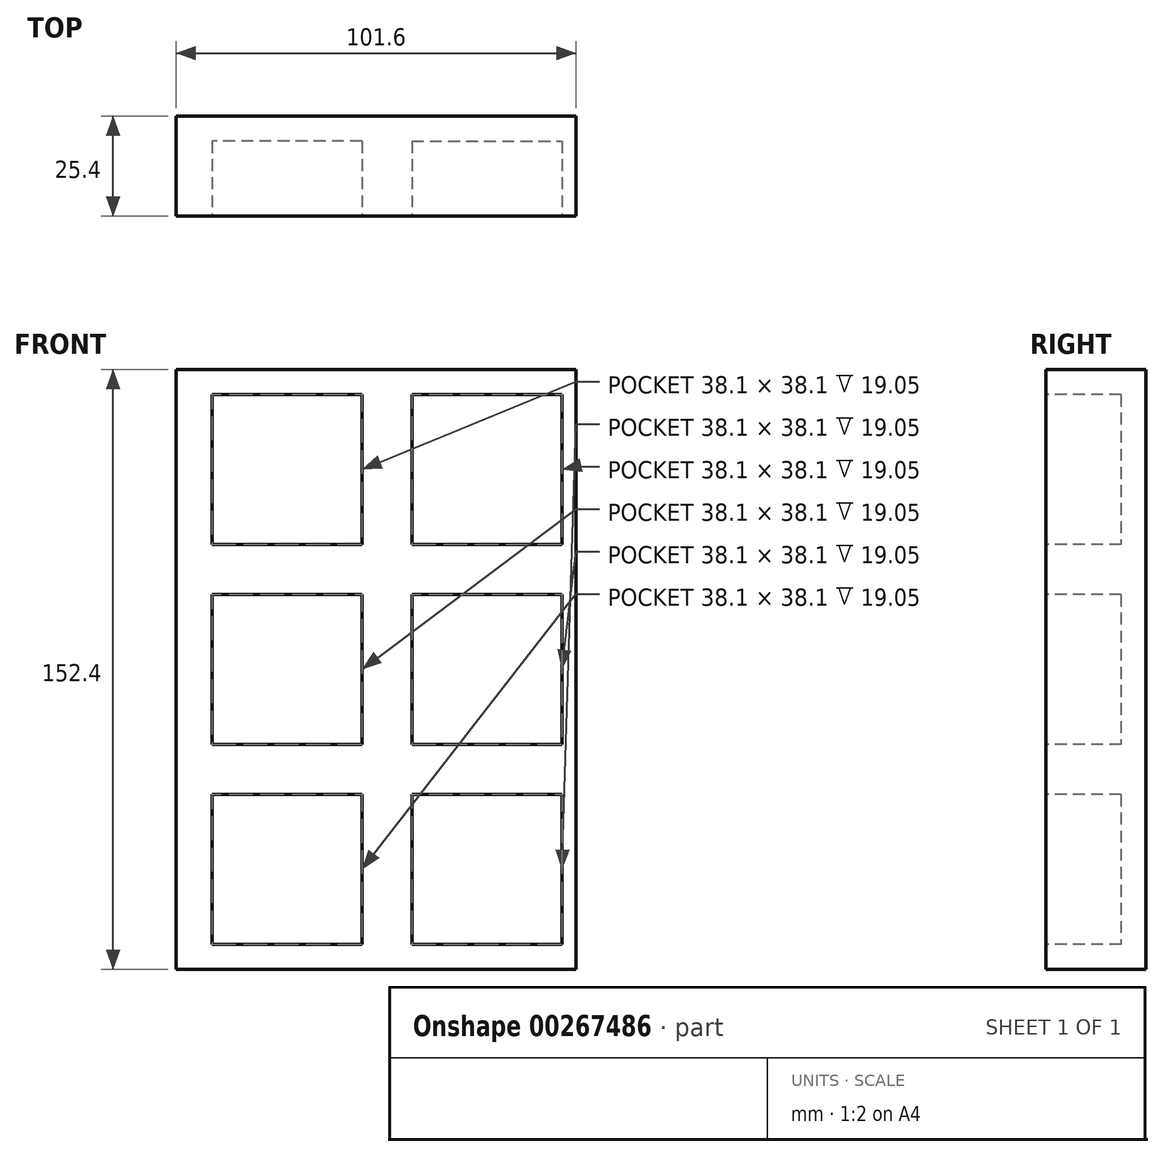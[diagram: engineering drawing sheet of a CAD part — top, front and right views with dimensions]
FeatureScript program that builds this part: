
annotation { "Feature Type Name" : "Feature", "Feature Type Description" : "" }
export const myFeature = defineFeature(function(context is Context, id is Id, definition is map)
    precondition{}
    {
        {
            var Q0;
            Q0=qCreatedBy(makeId("Front.planeOp"),FACE);
            var sketch = newSketch(context, id + "F0", { "sketchPlane" : qUnion([Q0])});
            skLineSegment(sketch, "E0.bottom", {"start": v(48.06, 76.2) * mm, "end": v(-53.54, 76.2) * mm});
            skLineSegment(sketch, "E0.top", {"start": v(48.06, -76.2) * mm, "end": v(-53.54, -76.2) * mm});
            skLineSegment(sketch, "E0.left", {"start": v(48.06, 76.2) * mm, "end": v(48.06, -76.2) * mm});
            skLineSegment(sketch, "E0.right", {"start": v(-53.54, 76.2) * mm, "end": v(-53.54, -76.2) * mm});
            skPoint(sketch, "E0.middle", {"position": v(-2.74, 0) * mm});
            skSolve(sketch);
        }
        {
            var Q0;
            Q0=makeQuery(id+"F0.imprint","IMPRINT",FACE,{"disambiguationData":[TD([[makeQuery(id+"F0.imprint","IMPRINT",EDGE,{"derivedFrom":sQuery(id+"F0.wireOp",EDGE,"E0.bottom")}),1.0]])]});
            extrude(context, id + "F1", {"entities" : qUnion([Q0]), "depth" : 25.4 * mm});
        }
        {
            var Q0;
            Q0=makeQuery(id+"F1.opExtrude","CAP_FACE",FACE,{"disambiguationData":[OSD([sQuery(id+"F0.wireOp",EDGE,"E0.bottom"),sQuery(id+"F0.wireOp",EDGE,"E0.top"),sQuery(id+"F0.wireOp",EDGE,"E0.left"),sQuery(id+"F0.wireOp",EDGE,"E0.right")])],"isStart":false});
            var sketch = newSketch(context, id + "F2", { "sketchPlane" : qUnion([Q0])});
            skLineSegment(sketch, "E1.bottom", {"start": v(6.35, 76.2) * mm, "end": v(-6.35, 76.2) * mm});
            skLineSegment(sketch, "E1.top", {"start": v(6.35, -76.2) * mm, "end": v(-6.35, -76.2) * mm});
            skPoint(sketch, "E1.middle", {"position": v(0, 0) * mm});
            skLineSegment(sketch, "E2.bottom", {"start": v(-53.54, 76.2) * mm, "end": v(48.06, 76.2) * mm});
            skLineSegment(sketch, "E2.left", {"start": v(-53.54, 76.2) * mm, "end": v(-53.54, 68.45) * mm});
            skLineSegment(sketch, "E2.right", {"start": v(48.06, 76.2) * mm, "end": v(48.06, 68.45) * mm});
            skLineSegment(sketch, "E3.bottom", {"start": v(-53.54, -76.2) * mm, "end": v(48.06, -76.2) * mm});
            skLineSegment(sketch, "E3.left", {"start": v(-53.54, -76.2) * mm, "end": v(-53.54, -63.5) * mm});
            skLineSegment(sketch, "E3.right", {"start": v(48.06, -76.2) * mm, "end": v(48.06, -63.5) * mm});
            skLineSegment(sketch, "E4.bottom", {"start": v(-53.54, 76.2) * mm, "end": v(-47.2, 76.2) * mm});
            skLineSegment(sketch, "E4.top", {"start": v(-53.54, -76.2) * mm, "end": v(-47.2, -76.2) * mm});
            skLineSegment(sketch, "E4.left", {"start": v(-53.54, 76.2) * mm, "end": v(-53.54, -76.2) * mm});
            skLineSegment(sketch, "E5.bottom", {"start": v(48.06, -76.2) * mm, "end": v(41.7, -76.2) * mm});
            skLineSegment(sketch, "E5.top", {"start": v(48.06, 76.2) * mm, "end": v(41.7, 76.2) * mm});
            skLineSegment(sketch, "E5.left", {"start": v(48.06, -76.2) * mm, "end": v(48.06, 76.2) * mm});
            skLineSegment(sketch, "E6.bottom", {"start": v(-6.35, 19.05) * mm, "end": v(-44.45, 19.05) * mm});
            skLineSegment(sketch, "E6.top", {"start": v(-6.35, -19.05) * mm, "end": v(-44.45, -19.05) * mm});
            skLineSegment(sketch, "E6.left", {"start": v(-6.35, 19.05) * mm, "end": v(-6.35, -19.05) * mm});
            skLineSegment(sketch, "E6.right", {"start": v(-44.45, 19.05) * mm, "end": v(-44.45, -19.05) * mm});
            skPoint(sketch, "E6.middle", {"position": v(-25.4, 0) * mm});
            skPoint(sketch, "E7.endSnap0", {"position": v(-25.4, -19.05) * mm});
            skLineSegment(sketch, "E8.bottom", {"start": v(-6.35, -31.75) * mm, "end": v(-44.45, -31.75) * mm});
            skLineSegment(sketch, "E8.top", {"start": v(-6.35, -69.85) * mm, "end": v(-44.45, -69.85) * mm});
            skLineSegment(sketch, "E8.left", {"start": v(-6.35, -31.75) * mm, "end": v(-6.35, -69.85) * mm});
            skLineSegment(sketch, "E8.right", {"start": v(-44.45, -31.75) * mm, "end": v(-44.45, -69.85) * mm});
            skPoint(sketch, "E8.middle", {"position": v(-25.4, -50.8) * mm});
            skLineSegment(sketch, "E9.bottom", {"start": v(-6.35, 69.85) * mm, "end": v(-44.45, 69.85) * mm});
            skLineSegment(sketch, "E9.top", {"start": v(-6.35, 31.75) * mm, "end": v(-44.45, 31.75) * mm});
            skLineSegment(sketch, "E9.left", {"start": v(-6.35, 69.85) * mm, "end": v(-6.35, 31.75) * mm});
            skLineSegment(sketch, "E9.right", {"start": v(-44.45, 69.85) * mm, "end": v(-44.45, 31.75) * mm});
            skPoint(sketch, "E9.middle", {"position": v(-25.4, 50.8) * mm});
            skPoint(sketch, "E10.MirrorP", {"position": v(25.4, -50.8) * mm});
            skLineSegment(sketch, "E11.MirrorCS", {"start": v(6.35, -19.05) * mm, "end": v(44.45, -19.05) * mm});
            skLineSegment(sketch, "E12.MirrorCS", {"start": v(44.45, -31.75) * mm, "end": v(44.45, -69.85) * mm});
            skLineSegment(sketch, "E13.MirrorCS", {"start": v(6.35, 69.85) * mm, "end": v(6.35, 31.75) * mm});
            skLineSegment(sketch, "E14.MirrorCS", {"start": v(6.35, -69.85) * mm, "end": v(44.45, -69.85) * mm});
            skLineSegment(sketch, "E15.MirrorCS", {"start": v(44.45, 69.85) * mm, "end": v(44.45, 31.75) * mm});
            skLineSegment(sketch, "E16.MirrorCS", {"start": v(6.35, 19.05) * mm, "end": v(44.45, 19.05) * mm});
            skLineSegment(sketch, "E17.MirrorCS", {"start": v(6.35, -31.75) * mm, "end": v(44.45, -31.75) * mm});
            skPoint(sketch, "E18.MirrorP", {"position": v(25.4, -19.05) * mm});
            skPoint(sketch, "E19.MirrorP", {"position": v(25.4, 50.8) * mm});
            skPoint(sketch, "E20.MirrorP", {"position": v(25.4, 0) * mm});
            skLineSegment(sketch, "E21.MirrorCS", {"start": v(6.35, 69.85) * mm, "end": v(44.45, 69.85) * mm});
            skLineSegment(sketch, "E22.MirrorCS", {"start": v(6.35, 19.05) * mm, "end": v(6.35, -19.05) * mm});
            skLineSegment(sketch, "E23.MirrorCS", {"start": v(6.35, -31.75) * mm, "end": v(6.35, -69.85) * mm});
            skLineSegment(sketch, "E24.MirrorCS", {"start": v(6.35, 31.75) * mm, "end": v(44.45, 31.75) * mm});
            skLineSegment(sketch, "E25.MirrorCS", {"start": v(44.45, 19.05) * mm, "end": v(44.45, -19.05) * mm});
            skSolve(sketch);
        }
        {
            var Q0;
            Q0=makeQuery(id+"F2.imprint","IMPRINT",FACE,{"disambiguationData":[TD([[makeQuery(id+"F2.imprint","IMPRINT",EDGE,{"derivedFrom":sQuery(id+"F2.wireOp",EDGE,"E9.bottom")}),1.0]])]});
            var Q1;
            Q1=makeQuery(id+"F2.imprint","IMPRINT",FACE,{"disambiguationData":[TD([[makeQuery(id+"F2.imprint","IMPRINT",EDGE,{"derivedFrom":sQuery(id+"F2.wireOp",EDGE,"E13.MirrorCS")}),1.0]])]});
            var Q2;
            Q2=makeQuery(id+"F2.imprint","IMPRINT",FACE,{"disambiguationData":[TD([[makeQuery(id+"F2.imprint","IMPRINT",EDGE,{"derivedFrom":sQuery(id+"F2.wireOp",EDGE,"E6.bottom")}),1.0]])]});
            var Q3;
            Q3=makeQuery(id+"F2.imprint","IMPRINT",FACE,{"disambiguationData":[TD([[makeQuery(id+"F2.imprint","IMPRINT",EDGE,{"derivedFrom":sQuery(id+"F2.wireOp",EDGE,"E11.MirrorCS")}),1.0]])]});
            var Q4;
            Q4=makeQuery(id+"F2.imprint","IMPRINT",FACE,{"disambiguationData":[TD([[makeQuery(id+"F2.imprint","IMPRINT",EDGE,{"derivedFrom":sQuery(id+"F2.wireOp",EDGE,"E8.bottom")}),1.0]])]});
            var Q5;
            Q5=makeQuery(id+"F2.imprint","IMPRINT",FACE,{"disambiguationData":[TD([[makeQuery(id+"F2.imprint","IMPRINT",EDGE,{"derivedFrom":sQuery(id+"F2.wireOp",EDGE,"E12.MirrorCS")}),-1.0]])]});
            extrude(context, id + "F3", {"entities" : qUnion([Q0, Q1, Q2, Q3, Q4, Q5]), "operationType" : NewBodyOperationType.REMOVE, "oppositeDirection" : true, "depth" : 19.05 * mm});
        }
    });
